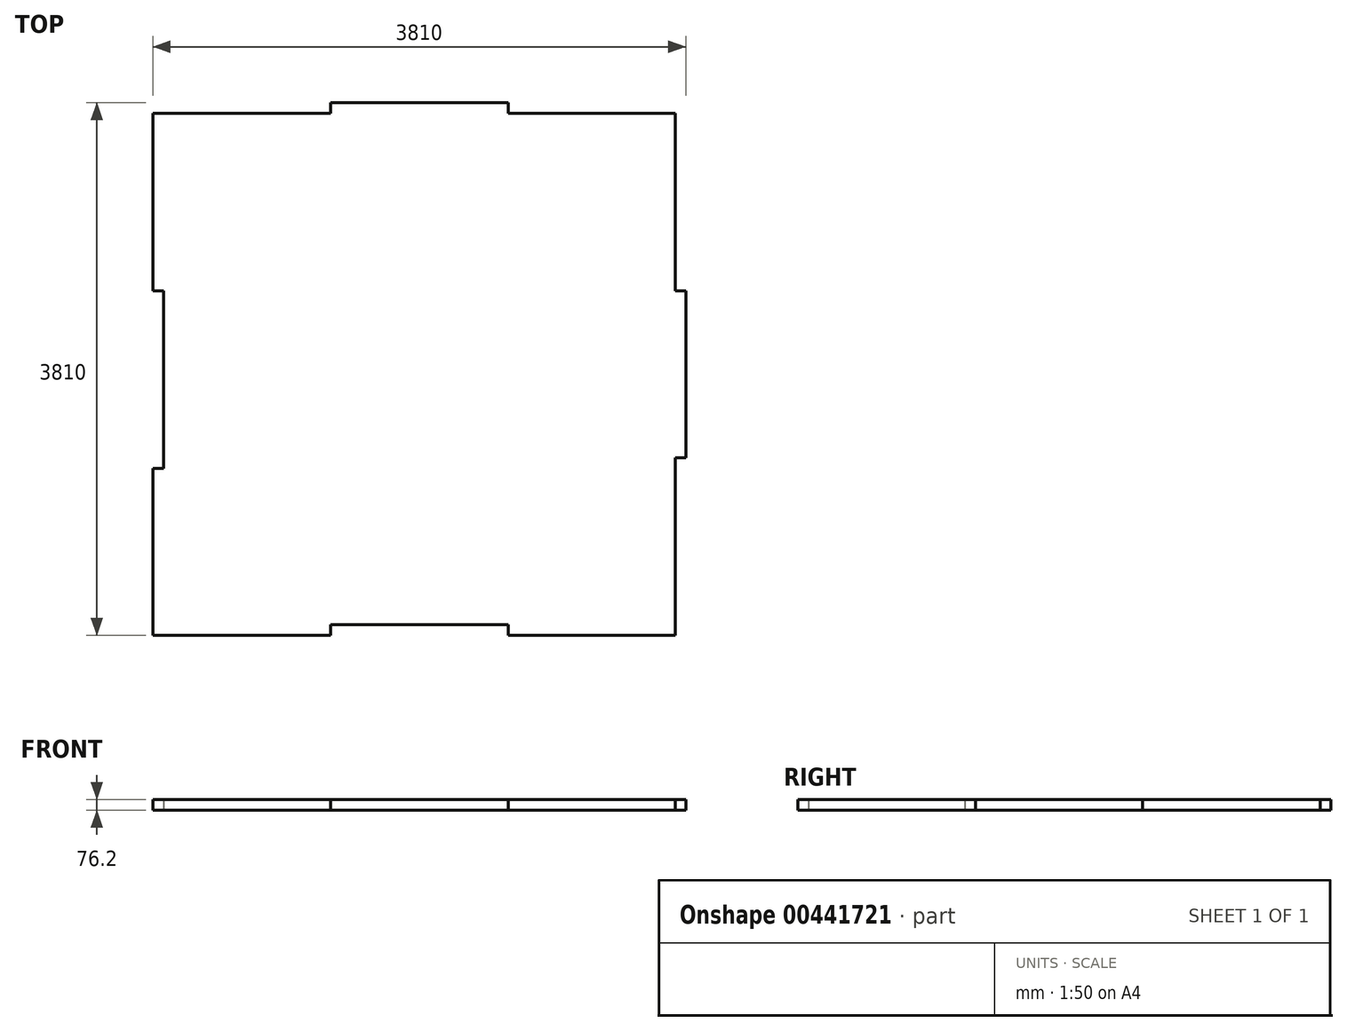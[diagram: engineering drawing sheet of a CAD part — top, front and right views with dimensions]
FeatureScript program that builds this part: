
annotation { "Feature Type Name" : "Feature", "Feature Type Description" : "" }
export const myFeature = defineFeature(function(context is Context, id is Id, definition is map)
    precondition{}
    {
        {
            var Q0;
            Q0=qCreatedBy(makeId("Top.planeOp"),FACE);
            var sketch = newSketch(context, id + "F0", { "sketchPlane" : qUnion([Q0])});
            skLineSegment(sketch, "E0.bottom", {"start": v(731.63, 1905) * mm, "end": v(-538.37, 1905) * mm});
            skLineSegment(sketch, "E0.top", {"start": v(1925.43, -1905) * mm, "end": v(731.63, -1905) * mm});
            skLineSegment(sketch, "E0.left", {"start": v(2001.63, 558.8) * mm, "end": v(2001.63, -635) * mm});
            skLineSegment(sketch, "E0.right", {"start": v(-1808.37, 1828.8) * mm, "end": v(-1808.37, 558.8) * mm});
            skPoint(sketch, "E0.middle", {"position": v(96.63, 0) * mm});
            skLineSegment(sketch, "E1", {"start": v(-1808.37, 1828.8) * mm, "end": v(-538.37, 1828.8) * mm});
            skLineSegment(sketch, "E2", {"start": v(-538.37, 1828.8) * mm, "end": v(-538.37, 1905) * mm});
            skLineSegment(sketch, "E3", {"start": v(1925.43, 1828.8) * mm, "end": v(731.63, 1828.8) * mm});
            skLineSegment(sketch, "E4", {"start": v(731.63, 1828.8) * mm, "end": v(731.63, 1905) * mm});
            skLineSegment(sketch, "E5", {"start": v(-1808.37, -1905) * mm, "end": v(-538.37, -1905) * mm});
            skLineSegment(sketch, "E6", {"start": v(-538.37, -1905) * mm, "end": v(-538.37, -1828.8) * mm});
            skLineSegment(sketch, "E7", {"start": v(-538.37, -1828.8) * mm, "end": v(731.63, -1828.8) * mm});
            skLineSegment(sketch, "E8", {"start": v(731.63, -1828.8) * mm, "end": v(731.63, -1905) * mm});
            skLineSegment(sketch, "E9.trimOffspring", {"start": v(-538.37, -1905) * mm, "end": v(-1808.37, -1905) * mm});
            skPoint(sketch, "E10.orphan", {"position": v(-1808.37, 1905) * mm});
            skPoint(sketch, "E11.orphan", {"position": v(2001.63, 1905) * mm});
            skLineSegment(sketch, "E12", {"start": v(-1808.37, 558.8) * mm, "end": v(-1732.17, 558.8) * mm});
            skLineSegment(sketch, "E13", {"start": v(-1732.17, 558.8) * mm, "end": v(-1732.17, -711.2) * mm});
            skLineSegment(sketch, "E14", {"start": v(-1732.17, -711.2) * mm, "end": v(-1808.37, -711.2) * mm});
            skLineSegment(sketch, "E15.trimOffspring", {"start": v(-1808.37, -711.2) * mm, "end": v(-1808.37, -1905) * mm});
            skLineSegment(sketch, "E16", {"start": v(1925.43, -1905) * mm, "end": v(1925.43, -635) * mm});
            skLineSegment(sketch, "E17", {"start": v(1925.43, -635) * mm, "end": v(2001.63, -635) * mm});
            skPoint(sketch, "E18.orphan", {"position": v(2001.63, -1905) * mm});
            skLineSegment(sketch, "E19", {"start": v(1925.43, 558.8) * mm, "end": v(2001.63, 558.8) * mm});
            skLineSegment(sketch, "E20", {"start": v(1925.43, 558.8) * mm, "end": v(1925.43, 1828.8) * mm});
            skSolve(sketch);
        }
        {
            var Q0;
            Q0=makeQuery(id+"F0.imprint","IMPRINT",FACE,{"disambiguationData":[TD([[makeQuery(id+"F0.imprint","IMPRINT",EDGE,{"derivedFrom":sQuery(id+"F0.wireOp",EDGE,"E0.bottom")}),1.0]])]});
            extrude(context, id + "F1", {"entities" : qUnion([Q0]), "depth" : 76.2 * mm});
        }
    });
